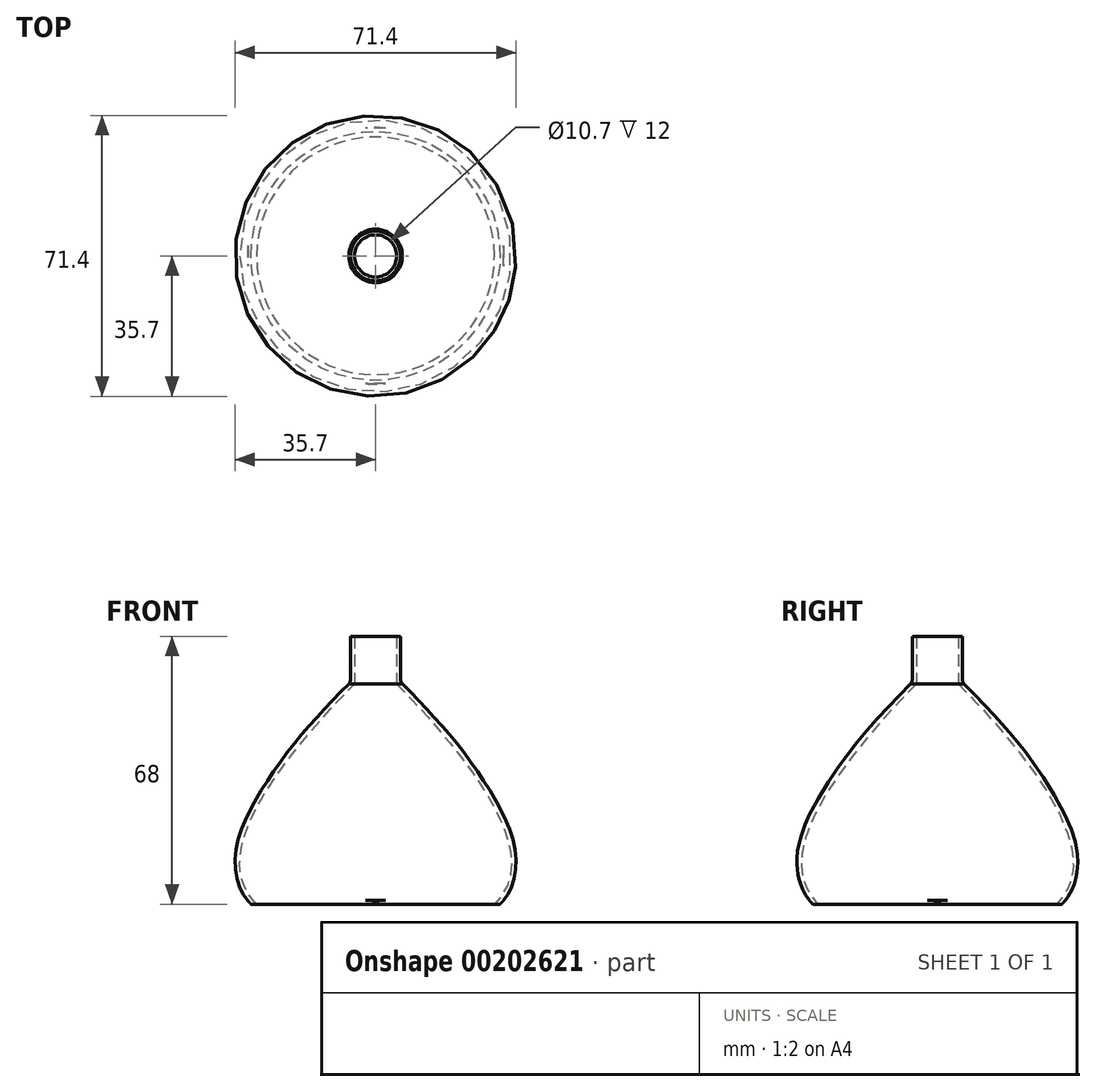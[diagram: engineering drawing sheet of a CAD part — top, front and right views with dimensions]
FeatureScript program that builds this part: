
annotation { "Feature Type Name" : "Feature", "Feature Type Description" : "" }
export const myFeature = defineFeature(function(context is Context, id is Id, definition is map)
    precondition{}
    {
        {
            var Q0;
            Q0=qCreatedBy(makeId("Front.planeOp"),FACE);
            var sketch = newSketch(context, id + "F0", { "sketchPlane" : qUnion([Q0])});
            skLineSegment(sketch, "E0", {"start": v(0, 0) * mm, "end": v(30.2, 0) * mm, "construction": true});
            skLineSegment(sketch, "E1", {"start": v(0, 0) * mm, "end": v(0, 56) * mm, "construction": true});
            skLineSegment(sketch, "E2", {"start": v(0, 56) * mm, "end": v(5.35, 56) * mm, "construction": true});
            skFitSpline(sketch, "E3", {"points": [v(30.2, 0) * mm, v(5.35, 56) * mm], "startDerivative": vector(34, 32.74) * mm, "endDerivative": vector(-72.7, 74.92) * mm});
            skLineSegment(sketch, "E4", {"start": v(5.35, 56) * mm, "end": v(5.35, 68) * mm});
            skLineSegment(sketch, "E5.0", {"start": v(6.35, 57.21) * mm, "end": v(6.35, 68) * mm});
            skLineSegment(sketch, "E6", {"start": v(5.35, 68) * mm, "end": v(6.35, 68) * mm});
            skLineSegment(sketch, "E7", {"start": v(30.2, 0) * mm, "end": v(39, 0) * mm});
            skLineSegment(sketch, "E8", {"start": v(39, 0) * mm, "end": v(39, 1) * mm});
            skLineSegment(sketch, "E9", {"start": v(39, 1) * mm, "end": v(32.45, 1) * mm});
            skFitSpline(sketch, "E10.trimOffspring", {"points": [v(30.9, -0.72) * mm, v(31.65, 0) * mm, v(32.97, 1.54) * mm, v(34.4, 4.08) * mm, v(35.26, 6.84) * mm, v(35.7, 10.77) * mm, v(34.98, 16.09) * mm, v(32.29, 23.06) * mm, v(27.94, 30.63) * mm, v(20.11, 41.49) * mm, v(12.14, 50.43) * mm, v(6.07, 56.7) * mm]});
            skPoint(sketch, "E11.visualSharp", {"position": v(6.35, 56.4) * mm});
            skArc(sketch, "E11.filletArc", {"start": v(6.35, 57.21) * mm, "mid": v(6.5, 56.47) * mm, "end": v(6.9, 55.83) * mm});
            skSolve(sketch);
        }
        {
            var Q0;
            Q0=makeQuery(id+"F0.imprint","IMPRINT",FACE,{"disambiguationData":[TD([[makeQuery(id+"F0.imprint","IMPRINT",EDGE,{"derivedFrom":sQuery(id+"F0.wireOp",EDGE,"E3")}),-1.0]])]});
            var Q1;
            Q1=sQuery(id+"F0.wireOp",EDGE,"E1");
            revolve(context, id + "F1", {"entities" : qUnion([Q0]), "axis" : qUnion([Q1]), "revolveType" : RevolveType.FULL});
        }
        {
            var Q0;
            Q0=qCreatedBy(makeId("Top.planeOp"),FACE);
            var sketch = newSketch(context, id + "F2", { "sketchPlane" : qUnion([Q0])});
            skLineSegment(sketch, "E12.bottom", {"start": v(-25, 25) * mm, "end": v(25, 25) * mm, "construction": true});
            skLineSegment(sketch, "E12.top", {"start": v(-25, -25) * mm, "end": v(25, -25) * mm, "construction": true});
            skLineSegment(sketch, "E12.left", {"start": v(-25, 25) * mm, "end": v(-25, -25) * mm, "construction": true});
            skLineSegment(sketch, "E12.right", {"start": v(25, 25) * mm, "end": v(25, -25) * mm, "construction": true});
            skPoint(sketch, "E12.middle", {"position": v(0, 0) * mm});
            skCircle(sketch, "E13", {"center": v(-25, 25) * mm, "radius": 2 * mm});
            skCircle(sketch, "E14", {"center": v(25, 25) * mm, "radius": 2 * mm});
            skCircle(sketch, "E15", {"center": v(25, -25) * mm, "radius": 2 * mm});
            skCircle(sketch, "E16", {"center": v(-25, -25) * mm, "radius": 2 * mm});
            skLineSegment(sketch, "E17.bottom", {"start": v(32.45, 32.45) * mm, "end": v(-32.45, 32.45) * mm});
            skLineSegment(sketch, "E17.top", {"start": v(32.45, -32.45) * mm, "end": v(-32.45, -32.45) * mm});
            skLineSegment(sketch, "E17.left", {"start": v(32.45, 32.45) * mm, "end": v(32.45, -32.45) * mm});
            skLineSegment(sketch, "E17.right", {"start": v(-32.45, 32.45) * mm, "end": v(-32.45, -32.45) * mm});
            skLineSegment(sketch, "E18.bottom", {"start": v(39.5, 39.5) * mm, "end": v(-39.5, 39.5) * mm});
            skLineSegment(sketch, "E18.top", {"start": v(39.5, -39.5) * mm, "end": v(-39.5, -39.5) * mm});
            skLineSegment(sketch, "E18.left", {"start": v(39.5, 39.5) * mm, "end": v(39.5, -39.5) * mm});
            skLineSegment(sketch, "E18.right", {"start": v(-39.5, 39.5) * mm, "end": v(-39.5, -39.5) * mm});
            skSolve(sketch);
        }
        {
            var Q0;
            Q0=makeQuery(id+"F2.imprint","IMPRINT",FACE,{"disambiguationData":[TD([[makeQuery(id+"F2.imprint","IMPRINT",EDGE,{"derivedFrom":sQuery(id+"F2.wireOp",EDGE,"E14")}),1.0]])]});
            var Q1;
            Q1=makeQuery(id+"F2.imprint","IMPRINT",FACE,{"disambiguationData":[TD([[makeQuery(id+"F2.imprint","IMPRINT",EDGE,{"derivedFrom":sQuery(id+"F2.wireOp",EDGE,"E13")}),1.0]])]});
            var Q2;
            Q2=makeQuery(id+"F2.imprint","IMPRINT",FACE,{"disambiguationData":[TD([[makeQuery(id+"F2.imprint","IMPRINT",EDGE,{"derivedFrom":sQuery(id+"F2.wireOp",EDGE,"E16")}),1.0]])]});
            var Q3;
            Q3=makeQuery(id+"F2.imprint","IMPRINT",FACE,{"disambiguationData":[TD([[makeQuery(id+"F2.imprint","IMPRINT",EDGE,{"derivedFrom":sQuery(id+"F2.wireOp",EDGE,"E15")}),1.0]])]});
            var Q4;
            Q4=makeQuery(id+"F2.imprint","IMPRINT",FACE,{"disambiguationData":[TD([[makeQuery(id+"F2.imprint","IMPRINT",EDGE,{"derivedFrom":sQuery(id+"F2.wireOp",EDGE,"E17.bottom")}),-1.0]])]});
            extrude(context, id + "F3", {"entities" : qUnion([Q0, Q1, Q2, Q3, Q4]), "operationType" : NewBodyOperationType.REMOVE, "depth" : 1 * mm});
        }
    });
